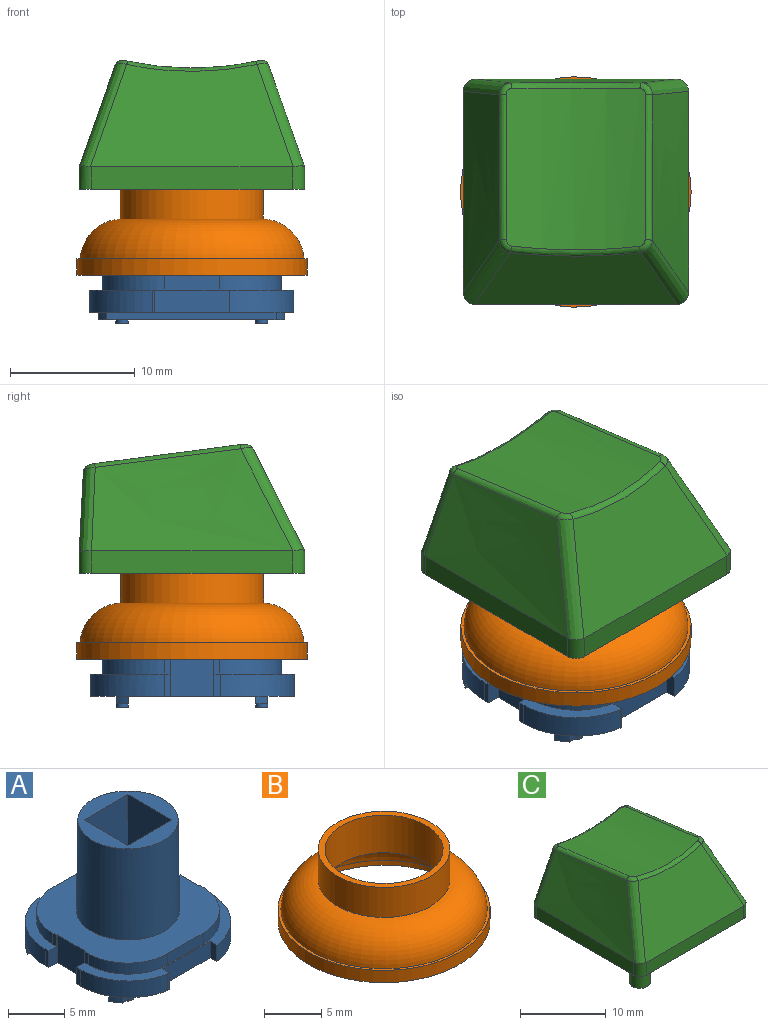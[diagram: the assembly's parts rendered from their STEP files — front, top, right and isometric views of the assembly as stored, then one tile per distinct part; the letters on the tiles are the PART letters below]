
ASSEMBLY  parts=3 mates=2
PART A: 86 faces, bbox 16.4x16.4x13.7 mm
  f0: plane 6x1.8mm, normal (0,1,0), area 10.8mm2, adj f3,f10,f11,f12
  f1: plane 1x1mm, normal (0,0,-1), area 0.8mm2, adj f13
  f2: plane 1x1mm, normal (0,0,-1), area 0.8mm2, adj f14
  f3: plane 1.8x0.85mm, normal (1,0,0), area 1.5mm2, adj f0,f11,f12,f26
  f4: plane 1.2x0.45mm, normal (-1,0,0), area 0.5mm2, adj f5,f11,f27,f28
  f5: revolved ~5x5mm, area 9.4mm2, adj f4,f6,f11,f28
  f6: plane 4.4x1.2mm, normal (0,1,0), area 5.3mm2, adj f5,f7,f11,f28
  f7: revolved ~5x5mm, area 9.4mm2, adj f6,f9,f11,f28
  f8: revolved ~9.8x9.13mm, area 277.6mm2, adj f19,f28
  f9: plane 1.2x0.45mm, normal (1,0,0), area 0.5mm2, adj f7,f11,f28,f29
  f10: plane 1.8x0.85mm, normal (-1,0,0), area 1.5mm2, adj f0,f11,f12,f31
  f11: plane 16.4x6.4mm, normal (0,0,1), area 17.2mm2, adj f0,f3,f4,f5,f6,f7,f9,f10
  f12: plane 13.52x2.05mm, normal (0,0,-1), area 17.2mm2, adj f0,f3,f10,f15,f26,f31
  f13: revolved ~1x1mm, area 0.9mm2, adj f1,f32,f33
  f14: revolved ~1x1mm, area 0.9mm2, adj f2,f33,f34
  f15: plane 13.52x0.6mm, normal (0,1,0), area 8.1mm2, adj f12,f32,f33,f34,f35,f36
  f16: plane 2.8x0.75mm, normal (0,0,-1), area 2.1mm2, adj f40,f41,f42,f43
  f17: plane 2.8x0.75mm, normal (0,0,-1), area 2.1mm2, adj f44,f45,f46,f47
  f18: plane 2.8x0.75mm, normal (0,0,-1), area 2.1mm2, adj f48,f49,f50,f51
  f19: plane 8.9x8.9mm, normal (0,0,1), area 32mm2, adj f8,f43,f47,f51,f52
  f20: plane 2.8x0.75mm, normal (0,0,-1), area 2.1mm2, adj f37,f38,f39,f52
  f21: revolved ~5x5mm, area 9.4mm2, adj f22,f24,f28,f55
  f22: plane 4.4x1.2mm, normal (0,-1,0), area 5.3mm2, adj f21,f23,f28,f55
  f23: revolved ~5x5mm, area 9.4mm2, adj f22,f28,f53,f55
  f24: plane 1.2x0.45mm, normal (1,0,0), area 0.5mm2, adj f21,f28,f55,f57
  f25: plane 1.8x0.45mm, normal (-1,0,0), area 0.8mm2, adj f11,f26,f27,f58
  f26: revolved ~5.95x5.2mm, area 15.5mm2, adj f3,f11,f12,f25,f35,f58
  f27: plane 3x1.1mm, normal (0,-1,0), area 2.1mm2, adj f4,f11,f25,f28,f58,f59,f72
  f28: plane 14.4x14.4mm, normal (0,0,1), area 119.7mm2, adj f4,f5,f6,f7,f8,f9,f21,f22
  f29: plane 3x1.1mm, normal (0,-1,0), area 2.1mm2, adj f9,f11,f28,f30,f60,f61,f72
  f30: plane 1.8x0.45mm, normal (1,0,0), area 0.8mm2, adj f11,f29,f31,f61
  f31: revolved ~5.95x5.2mm, area 15.5mm2, adj f10,f11,f12,f30,f36,f61
  f32: plane 1.86x1mm, normal (0,0,-1), area 1.1mm2, adj f13,f15,f36,f62
  f33: plane 11.2x1mm, normal (0,0,-1), area 10.4mm2, adj f13,f14,f15,f62
  f34: plane 1.85x1mm, normal (0,0,-1), area 1.1mm2, adj f14,f15,f35,f62
  f35: revolved ~1x0.69mm, area 0.7mm2, adj f15,f26,f34,f62
  f36: revolved ~1x0.69mm, area 0.7mm2, adj f15,f31,f32,f62
  f37: plane 5.9x0.75mm, normal (0,1,0), area 4.4mm2, adj f20,f38,f52,f63
  f38: plane 5.9x2.8mm, normal (1,0,0), area 16.5mm2, adj f20,f37,f39,f63
  f39: plane 5.9x0.75mm, normal (0,-1,0), area 4.4mm2, adj f20,f38,f52,f63
  f40: plane 5.9x0.75mm, normal (1,0,0), area 4.4mm2, adj f16,f41,f43,f63
  f41: plane 5.9x2.8mm, normal (0,-1,0), area 16.5mm2, adj f16,f40,f42,f63
  f42: plane 5.9x0.75mm, normal (-1,0,0), area 4.4mm2, adj f16,f41,f43,f63
  f43: plane 12.8x5.5mm, normal (0,-1,0), area 53.9mm2, adj f16,f19,f40,f42,f47,f52,f63
  f44: plane 5.9x0.75mm, normal (0,-1,0), area 4.4mm2, adj f17,f45,f47,f63
  f45: plane 5.9x2.8mm, normal (-1,0,0), area 16.5mm2, adj f17,f44,f46,f63
  f46: plane 5.9x0.75mm, normal (0,1,0), area 4.4mm2, adj f17,f45,f47,f63
  f47: plane 12.8x5.5mm, normal (-1,0,0), area 53.9mm2, adj f17,f19,f43,f44,f46,f51,f63
  f48: plane 5.9x0.75mm, normal (-1,0,0), area 4.4mm2, adj f18,f49,f51,f63
  f49: plane 5.9x2.8mm, normal (0,1,0), area 16.5mm2, adj f18,f48,f50,f63
  f50: plane 5.9x0.75mm, normal (1,0,0), area 4.4mm2, adj f18,f49,f51,f63
  f51: plane 12.8x5.5mm, normal (0,1,0), area 53.9mm2, adj f18,f19,f47,f48,f50,f52,f63
  f52: plane 12.8x5.5mm, normal (1,0,0), area 53.9mm2, adj f19,f20,f37,f39,f43,f51,f63
  f53: plane 1.2x0.45mm, normal (-1,0,0), area 0.5mm2, adj f23,f28,f55,f64
  f54: plane 1.8x0.2mm, normal (0,-1,0), area 0.4mm2, adj f55,f66,f70,f77
  f55: plane 16.4x6.45mm, normal (0,0,1), area 17.6mm2, adj f21,f22,f23,f24,f53,f54,f56,f57
  f56: plane 1.8x0.45mm, normal (1,0,0), area 0.8mm2, adj f55,f57,f69,f71
  f57: plane 3x1.1mm, normal (0,1,0), area 2.1mm2, adj f24,f28,f55,f56,f60,f71,f72
  f58: plane 3.35x1.93mm, normal (0,0,-1), area 3.5mm2, adj f25,f26,f27,f62,f72
  f59: plane 3.5x3mm, normal (-1,0,0), area 10.5mm2, adj f27,f28,f64,f72
  f60: plane 3.5x3mm, normal (1,0,0), area 10.5mm2, adj f28,f29,f57,f72
  f61: plane 3.35x1.93mm, normal (0,0,-1), area 3.5mm2, adj f29,f30,f31,f62,f72
  f62: plane 14.91x0.6mm, normal (0,-1,0), area 8.9mm2, adj f32,f33,f34,f35,f36,f58,f61,f72
  f63: plane 9.2x9.2mm, normal (0,0,-1), area 27.8mm2, adj f37,f38,f39,f40,f41,f42,f43,f44
  f64: plane 3x1.1mm, normal (0,1,0), area 2.1mm2, adj f28,f53,f55,f59,f65,f72,f73
  f65: plane 1.8x0.53mm, normal (-1,0,0), area 1mm2, adj f55,f64,f70,f73
  f66: plane 1.8x0.9mm, normal (1,0,0), area 1.6mm2, adj f54,f55,f67,f77
  f67: plane 6x1.8mm, normal (0,-1,0), area 10.8mm2, adj f55,f66,f68,f77
  f68: plane 1.8x0.85mm, normal (-1,0,0), area 1.5mm2, adj f55,f67,f69,f77
  f69: revolved ~5.95x5.2mm, area 15.5mm2, adj f55,f56,f68,f71,f75,f77
  f70: revolved ~5.92x5mm, area 15.2mm2, adj f54,f55,f65,f73,f77,f78
  f71: plane 3.35x1.93mm, normal (0,0,-1), area 3.5mm2, adj f56,f57,f69,f72,f79
  f72: plane 14.4x10.2mm, normal (0,0,-1), area 76.3mm2, adj f27,f29,f57,f58,f59,f60,f61,f62
  f73: plane 3.35x1.93mm, normal (0,0,-1), area 3.6mm2, adj f64,f65,f70,f72,f79
  f74: plane 1x1mm, normal (0,0,-1), area 0.8mm2, adj f80
  f75: revolved ~1x0.69mm, area 0.7mm2, adj f69,f76,f79,f81
  f76: plane 1.86x1mm, normal (0,0,-1), area 1.1mm2, adj f75,f79,f80,f81
  f77: plane 13.59x2.1mm, normal (0,0,-1), area 17.5mm2, adj f54,f66,f67,f68,f69,f70,f81
  f78: revolved ~1x0.67mm, area 0.7mm2, adj f70,f79,f81,f82
  f79: plane 14.95x0.6mm, normal (0,1,0), area 9mm2, adj f71,f72,f73,f75,f76,f78,f82,f83
  f80: revolved ~1x1mm, area 0.9mm2, adj f74,f76,f83
  f81: plane 13.59x0.6mm, normal (0,-1,0), area 8.2mm2, adj f75,f76,f77,f78,f82,f83
  f82: plane 1.9x1mm, normal (0,0,-1), area 1.2mm2, adj f78,f79,f81,f84
  f83: plane 11.2x1mm, normal (0,0,-1), area 10.4mm2, adj f79,f80,f81,f84
  f84: revolved ~1x1mm, area 0.9mm2, adj f82,f83,f85
  f85: plane 1x1mm, normal (0,0,-1), area 0.8mm2, adj f84
PART B: 9 faces, bbox 19.5x19.5x7.7 mm
  f0: cylinder r=9.25mm len=18.5mm, axis (0,0,1), area 76.2mm2, adj f1,f8
  f1: plane 18.5x18.5mm, normal (0,0,-1), area 41.8mm2, adj f0,f2
  f2: cylinder r=8.5mm len=17mm, axis (0,0,1), area 27.5mm2, adj f1,f3
  f3: torus R=5.16mm, axis (0,0,1), area 232.3mm2, adj f2,f4
  f4: cylinder r=5.15mm len=10.3mm, axis (0,0,1), area 129.4mm2, adj f3,f5
  f5: plane 11.5x11.5mm, normal (0,0,1), area 20.5mm2, adj f4,f6
  f6: cylinder r=5.75mm len=11.5mm, axis (0,0,1), area 115.6mm2, adj f5,f7
  f7: torus R=5.6mm, axis (0,0,1), area 243.6mm2, adj f6,f8
  f8: plane 18.5x18.5mm, normal (0,0,1), area 14.3mm2, adj f0,f7
PART C: 42 faces, bbox 21.1x23x22.5 mm
  f0: plane 18.1x18.1mm, normal (0,0,-1), area 67.5mm2, adj f1,f2,f3,f4,f10,f12,f14,f16
  f1: plane 16.1x1.8mm, normal (1,0,0), area 29mm2, adj f0,f8,f10,f16
  f2: plane 16.11x1.81mm, normal (0,1,0), area 29mm2, adj f0,f5,f14,f15,f16,f17
  f3: plane 16.1x1.8mm, normal (-1,0,0), area 29mm2, adj f0,f6,f12,f14
  f4: plane 16.1x1.8mm, normal (0,-1,0), area 29mm2, adj f0,f7,f10,f12
  f5: plane 15.97x6.36mm, normal (0,1,0.05), area 80mm2, adj f2,f15,f17,f20
  f6: bspline ~18.1x8.73mm, area 112.7mm2, adj f3,f12,f13,f14,f15,f19
  f7: plane 16.3x8.23mm, normal (0,-0.89,0.45), area 118.9mm2, adj f4,f10,f11,f12,f13,f23
  f8: bspline ~18.1x8.73mm, area 112.7mm2, adj f1,f10,f11,f16,f17,f24
  f9: cylinder r=22.9mm len=12.77mm, axis (0,0.99,-0.13), area 143.4mm2, adj f18,f19,f20,f21,f22,f23,f24,f25
  f10: cylinder r=1mm len=1.87mm, axis (0,0,-1), area 2.9mm2, adj f0,f1,f4,f7,f8,f11
  f11: bspline ~10.61x6.11mm, area 13.9mm2, adj f7,f8,f10,f25
  f12: cylinder r=1mm len=1.87mm, axis (0,0,1), area 2.9mm2, adj f0,f3,f4,f6,f7,f13
  f13: bspline ~10.63x6.12mm, area 13.9mm2, adj f6,f7,f12,f21
  f14: cylinder r=1mm len=1.81mm, axis (0,0,-1), area 2.8mm2, adj f0,f2,f3,f6,f15
  f15: bspline ~8.47x4.4mm, area 11mm2, adj f2,f5,f6,f14,f18
  f16: cylinder r=1mm len=1.81mm, axis (0,0,1), area 2.8mm2, adj f0,f1,f2,f8,f17
  f17: bspline ~8.46x4.39mm, area 11mm2, adj f2,f5,f8,f16,f22
  f18: bspline ~1.18x1.07mm, area 0.8mm2, adj f9,f15,f19,f20
  f19: bspline ~18.54x2.8mm, area 8.6mm2, adj f6,f9,f18,f21
  f20: bspline ~10.51x1.06mm, area 7.3mm2, adj f5,f9,f18,f22
  f21: bspline ~1.18x1.11mm, area 0.8mm2, adj f9,f13,f19,f23
  f22: bspline ~1.22x1.01mm, area 0.8mm2, adj f9,f17,f20,f24
  f23: bspline ~10.48x0.82mm, area 6.5mm2, adj f7,f9,f21,f25
  f24: bspline ~18.54x2.8mm, area 8.6mm2, adj f8,f9,f22,f25
  f25: bspline ~1.28x1.05mm, area 0.8mm2, adj f9,f11,f23,f24
  f26: plane 16.12x1.65mm, normal (-1,0,0), area 26mm2, adj f0,f27,f29,f32,f33
  f27: plane 16.1x1.77mm, normal (0,-1,0), area 28.6mm2, adj f0,f26,f28,f30,f31,f33
  f28: plane 16.12x1.65mm, normal (1,0,0), area 26mm2, adj f0,f27,f29,f31,f32
  f29: plane 16.1x1.56mm, normal (0,1,0), area 25.1mm2, adj f0,f26,f28,f32
  f30: plane 16.17x6.17mm, normal (0,-1,-0.05), area 75.1mm2, adj f27,f31,f33,f34
  f31: offset ~20.1x10.73mm, area 104.4mm2, adj f27,f28,f30,f32,f34
  f32: plane 16.52x8.13mm, normal (0,0.89,-0.45), area 111.3mm2, adj f26,f28,f29,f31,f33,f34
  f33: offset ~20.1x10.73mm, area 104.4mm2, adj f26,f27,f30,f32,f34
  f34: cylinder r=23.9mm len=11.98mm, axis (0,0.99,-0.13), area 102mm2, adj f30,f31,f32,f33,f36,f37,f38,f39
  f35: plane 5.3x5.3mm, normal (0,0,-1), area 23.6mm2, adj f36,f37,f38,f39,f40
  f36: plane 14.05x5.34mm, normal (0,1,0), area 73.7mm2, adj f34,f35,f37,f38
  f37: plane 14.7x5.3mm, normal (1,0,0), area 76.1mm2, adj f34,f35,f36,f39
  f38: plane 14.7x5.3mm, normal (-1,0,0), area 76.1mm2, adj f34,f35,f36,f39
  f39: plane 14.74x5.34mm, normal (0,-1,0), area 77.4mm2, adj f34,f35,f37,f38
  f40: cylinder r=1.2mm len=3.5mm, axis (0,0,1), area 26.4mm2, adj f35,f41
  f41: plane 2.4x2.4mm, normal (0,0,-1), area 4.5mm2, adj f40
PLACE A at identity fixed
PLACE B t=(0,0,3)mm
PLACE C t=(0,0,9.9)mm
MATE slider A.f19 <-> C.f40  axis (0,0,1) through (0,0,12.8)mm
MATE fastened A.f28 <-> B.f0  axis (0,0,1) through (0,0,3)mm
